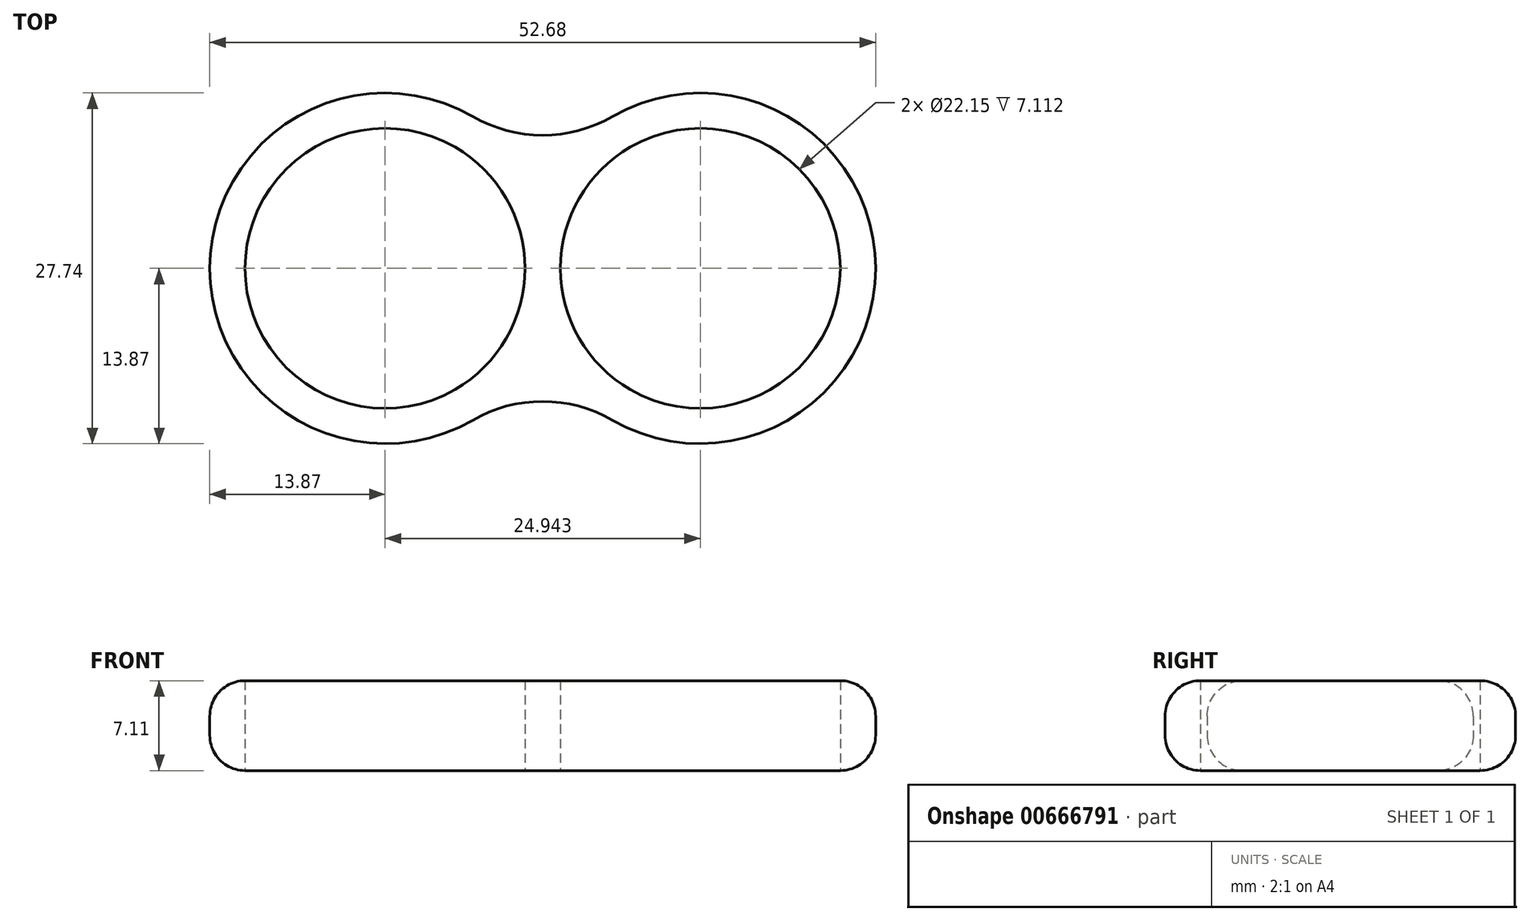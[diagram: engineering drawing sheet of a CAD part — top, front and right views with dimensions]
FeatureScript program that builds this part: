
annotation { "Feature Type Name" : "Feature", "Feature Type Description" : "" }
export const myFeature = defineFeature(function(context is Context, id is Id, definition is map)
    precondition{}
    {
        {
            var Q0;
            Q0=qCreatedBy(makeId("Top.planeOp"),FACE);
            var sketch = newSketch(context, id + "F0", { "sketchPlane" : qUnion([Q0])});
            skCircle(sketch, "E0", {"center": v(0, 0) * mm, "radius": 11.07 * mm});
            skCircle(sketch, "E1", {"center": v(24.94, 0) * mm, "radius": 11.07 * mm});
            skArc(sketch, "E2", {"start": v(6.93, 12.01) * mm, "mid": v(-13.87, 0) * mm, "end": v(6.93, -12.01) * mm});
            skArc(sketch, "E3", {"start": v(18, -12.01) * mm, "mid": v(38.81, 0) * mm, "end": v(18, 12.01) * mm});
            skArc(sketch, "E4", {"start": v(6.93, 12.01) * mm, "mid": v(12.47, 10.53) * mm, "end": v(18, 12.01) * mm});
            skArc(sketch, "E5", {"start": v(18, -12.01) * mm, "mid": v(12.47, -10.53) * mm, "end": v(6.93, -12.01) * mm});
            skSolve(sketch);
        }
        {
            var Q0;
            Q0 = qSketchRegion(id + "F0", true);
            extrude(context, id + "F1", {"entities" : qUnion([Q0]), "depth" : 7.11 * mm, "offsetDistance" : 25.4 * mm});
        }
        {
            var Q0;
            Q0=makeQuery(id+"F1.opExtrude","CAP_EDGE",EDGE,{"disambiguationData":[OSD([sQuery(id+"F0.wireOp",EDGE,"E3")])],"isStart":false});
            fillet(context, id + "F2", {"entities" : qUnion([Q0]), "radius" : 2.8 * mm, "tangentPropagation" : true, "allowEdgeOverflow" : false});
        }
        {
            var Q0;
            Q0=makeQuery(id+"F1.opExtrude","CAP_EDGE",EDGE,{"disambiguationData":[OSD([sQuery(id+"F0.wireOp",EDGE,"E2")])],"isStart":true});
            fillet(context, id + "F3", {"entities" : qUnion([Q0]), "radius" : 2.8 * mm, "tangentPropagation" : true, "allowEdgeOverflow" : false});
        }
    });
